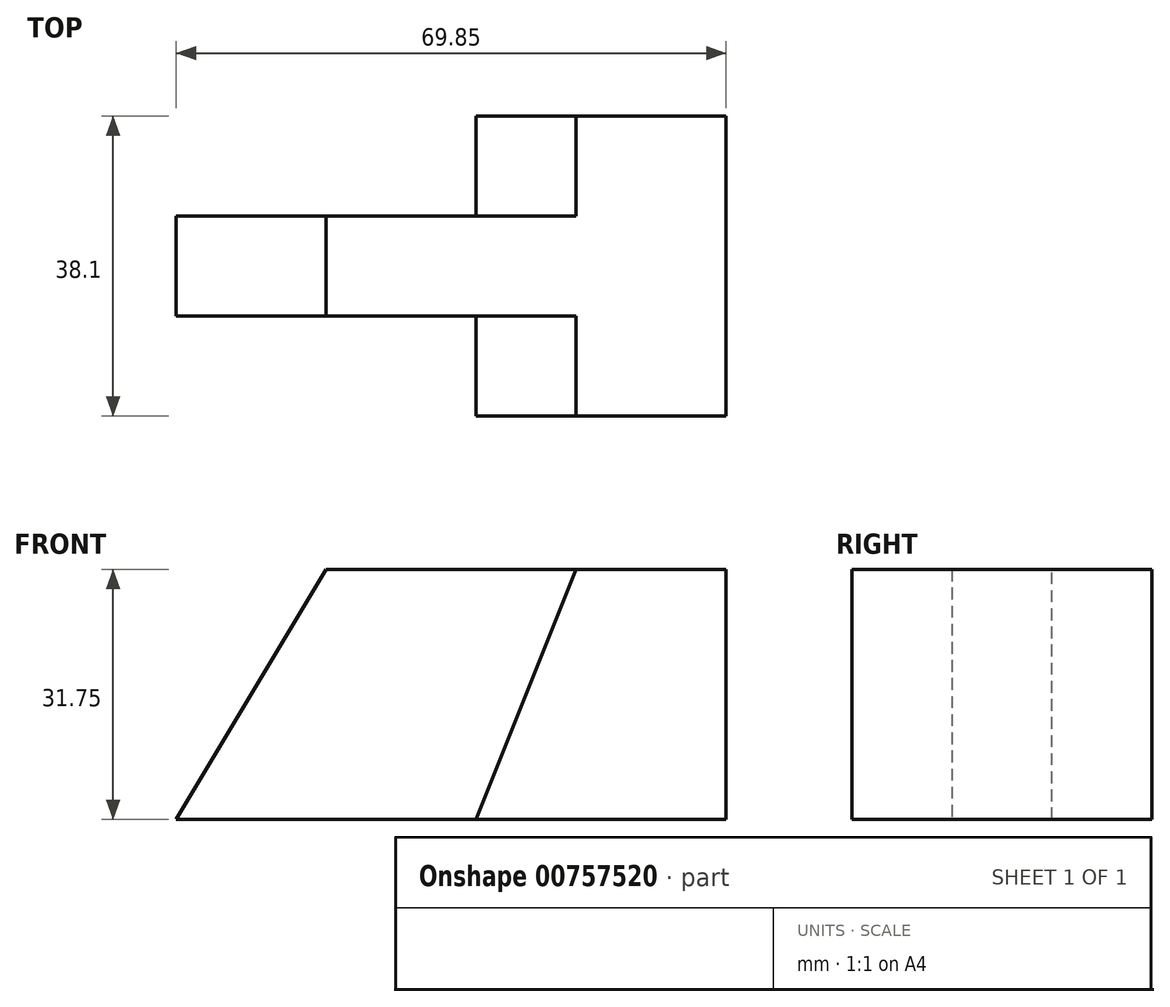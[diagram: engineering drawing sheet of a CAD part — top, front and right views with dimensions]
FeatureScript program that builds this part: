
annotation { "Feature Type Name" : "Feature", "Feature Type Description" : "" }
export const myFeature = defineFeature(function(context is Context, id is Id, definition is map)
    precondition{}
    {
        {
            var Q0;
            Q0=qCreatedBy(makeId("Front.planeOp"),FACE);
            var sketch = newSketch(context, id + "F0", { "sketchPlane" : qUnion([Q0])});
            skLineSegment(sketch, "E0", {"start": v(0, 0) * mm, "end": v(0, 31.75) * mm});
            skLineSegment(sketch, "E1", {"start": v(0, 31.75) * mm, "end": v(-69.85, 31.75) * mm});
            skLineSegment(sketch, "E2", {"start": v(-69.85, 31.75) * mm, "end": v(-69.85, 0) * mm});
            skLineSegment(sketch, "E3", {"start": v(-69.85, 0) * mm, "end": v(0, 0) * mm});
            skSolve(sketch);
        }
        {
            var Q0;
            Q0 = qSketchRegion(id + "F0", true);
            var Q1;
            Q1 = qSketchRegion(id + "F2", true);
            extrude(context, id + "F1", {"entities" : qUnion([Q0, Q1]), "depth" : 38.1 * mm, "offsetDistance" : 25.4 * mm});
        }
        {
            var Q0;
            Q0=makeQuery(id+"F1.opExtrude","CAP_FACE",FACE,{"disambiguationData":[OSD([sQuery(id+"F0.wireOp",EDGE,"E0"),sQuery(id+"F0.wireOp",EDGE,"E1"),sQuery(id+"F0.wireOp",EDGE,"E2"),sQuery(id+"F0.wireOp",EDGE,"E3")])],"isStart":true});
            var sketch = newSketch(context, id + "F2", { "sketchPlane" : qUnion([Q0])});
            skLineSegment(sketch, "E4", {"start": v(19.05, 31.75) * mm, "end": v(31.75, 0) * mm});
            skSolve(sketch);
        }
        {
            var Q0;
            {var subQ0=sQuery(id+"F2.wireOp",EDGE,"E4");Q0=makeQuery(id+"F2.imprint","IMPRINT",FACE,{"disambiguationData":[TD([[makeQuery(id+"F2.imprint","IMPRINT",EDGE,{"derivedFrom":subQ0}),1.0]])]});}
            extrude(context, id + "F3", {"entities" : qUnion([Q0]), "operationType" : NewBodyOperationType.REMOVE, "oppositeDirection" : true, "depth" : 12.7 * mm, "offsetDistance" : 25.4 * mm});
        }
        {
            var Q0;
            Q0=makeQuery(id+"F1.opExtrude","CAP_FACE",FACE,{"disambiguationData":[OSD([sQuery(id+"F0.wireOp",EDGE,"E0"),sQuery(id+"F0.wireOp",EDGE,"E1"),sQuery(id+"F0.wireOp",EDGE,"E2"),sQuery(id+"F0.wireOp",EDGE,"E3")])],"isStart":false});
            var sketch = newSketch(context, id + "F4", { "sketchPlane" : qUnion([Q0])});
            skLineSegment(sketch, "E5", {"start": v(-19.05, 31.75) * mm, "end": v(-31.75, 0) * mm});
            skSolve(sketch);
        }
        {
            var Q0;
            {var subQ0=sQuery(id+"F4.wireOp",EDGE,"E5");Q0=makeQuery(id+"F4.imprint","IMPRINT",FACE,{"disambiguationData":[TD([[makeQuery(id+"F4.imprint","IMPRINT",EDGE,{"derivedFrom":subQ0}),-1.0]])]});}
            extrude(context, id + "F5", {"entities" : qUnion([Q0]), "operationType" : NewBodyOperationType.REMOVE, "oppositeDirection" : true, "depth" : 12.7 * mm, "offsetDistance" : 25.4 * mm});
        }
        {
            var Q0;
            Q0=makeQuery(id+"F5.boolean.opBoolean","COPY",FACE,{"derivedFrom":makeQuery(id+"F5.opExtrude","CAP_FACE",FACE,{"disambiguationData":[OSD([sQuery(id+"F0.wireOp",EDGE,"E1"),sQuery(id+"F0.wireOp",EDGE,"E2"),sQuery(id+"F0.wireOp",EDGE,"E3"),sQuery(id+"F4.wireOp",EDGE,"E5")])],"isStart":false})});
            var sketch = newSketch(context, id + "F6", { "sketchPlane" : qUnion([Q0])});
            skLineSegment(sketch, "E6", {"start": v(-50.8, 31.75) * mm, "end": v(-69.85, 0) * mm});
            skPoint(sketch, "E6.startSnap0", {"position": v(-50.8, 0) * mm});
            skSolve(sketch);
        }
        {
            var Q0;
            {var subQ0=sQuery(id+"F6.wireOp",EDGE,"E6");Q0=makeQuery(id+"F6.imprint","IMPRINT",FACE,{"disambiguationData":[TD([[makeQuery(id+"F6.imprint","IMPRINT",EDGE,{"derivedFrom":subQ0}),-1.0]])]});}
            extrude(context, id + "F7", {"entities" : qUnion([Q0]), "operationType" : NewBodyOperationType.REMOVE, "endBound" : BoundingType.THROUGH_ALL, "oppositeDirection" : true, "depth" : 25.4 * mm, "offsetDistance" : 25.4 * mm});
        }
    });
